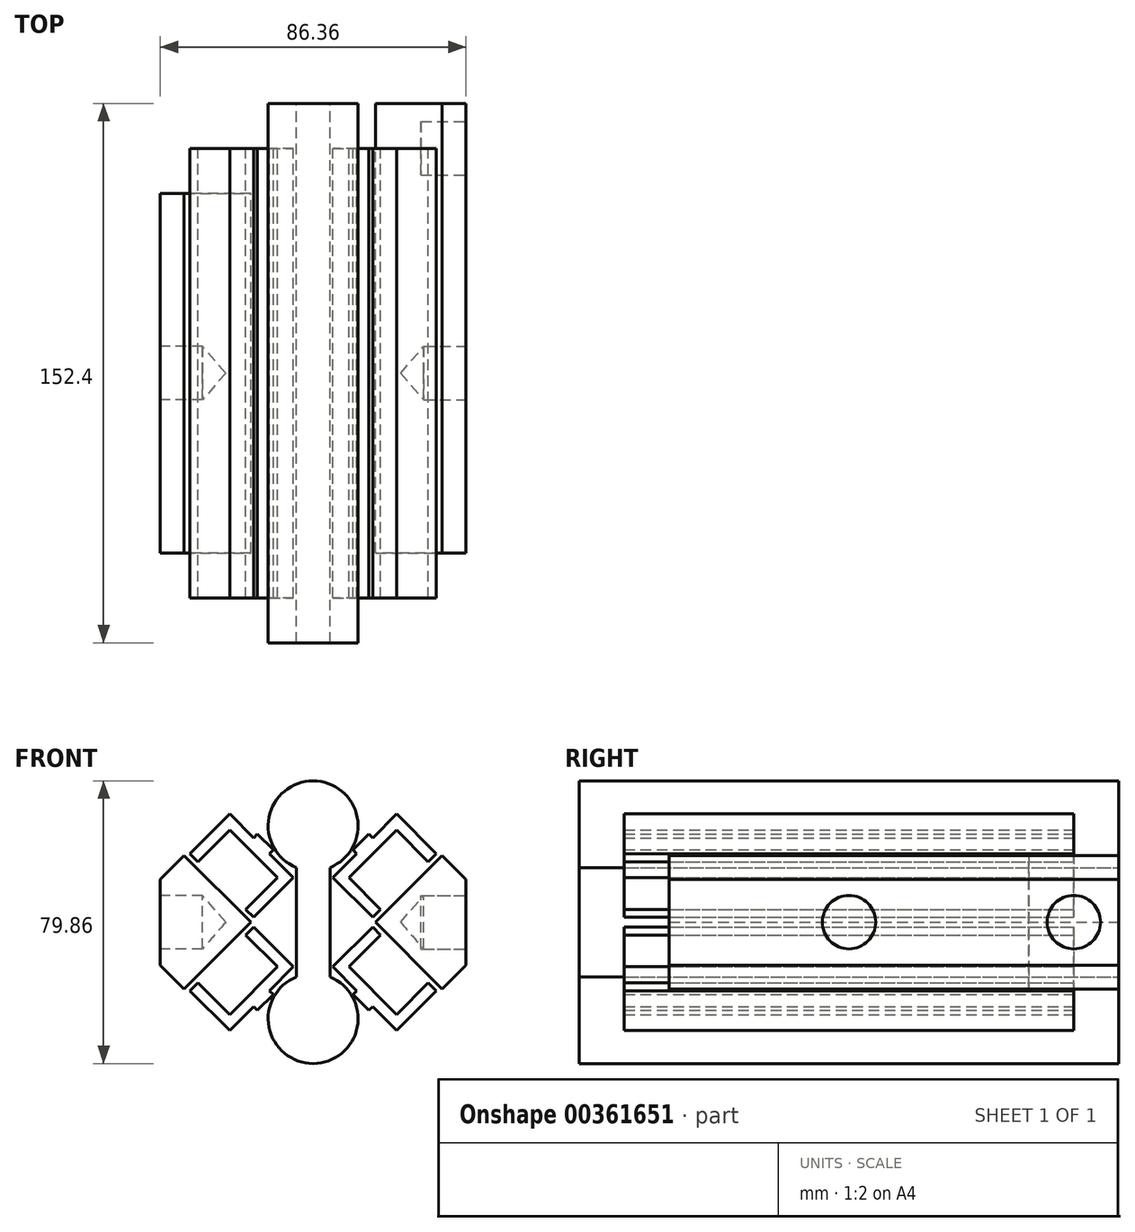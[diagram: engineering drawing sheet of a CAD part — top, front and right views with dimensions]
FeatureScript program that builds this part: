
annotation { "Feature Type Name" : "Feature", "Feature Type Description" : "" }
export const myFeature = defineFeature(function(context is Context, id is Id, definition is map)
    precondition{}
    {
        {
            var Q0;
            Q0=qCreatedBy(makeId("Front.planeOp"),FACE);
            var sketch = newSketch(context, id + "F0", { "sketchPlane" : qUnion([Q0])});
            skLineSegment(sketch, "E0", {"start": v(32.53, 17.1) * mm, "end": v(34.77, 19.34) * mm});
            skLineSegment(sketch, "E1", {"start": v(34.77, 19.34) * mm, "end": v(23.55, 30.57) * mm});
            skLineSegment(sketch, "E2", {"start": v(23.55, 30.57) * mm, "end": v(16.81, 23.84) * mm});
            skLineSegment(sketch, "E3", {"start": v(5.59, 12.6) * mm, "end": v(16.81, 1.38) * mm});
            skLineSegment(sketch, "E4", {"start": v(16.81, 1.38) * mm, "end": v(19.06, 3.63) * mm});
            skLineSegment(sketch, "E5", {"start": v(19.06, 3.63) * mm, "end": v(10.08, 12.6) * mm});
            skLineSegment(sketch, "E6", {"start": v(10.08, 12.6) * mm, "end": v(23.55, 26.08) * mm});
            skLineSegment(sketch, "E7", {"start": v(23.55, 26.08) * mm, "end": v(32.53, 17.1) * mm});
            skLineSegment(sketch, "E8", {"start": v(10.08, 12.6) * mm, "end": v(7.83, 10.36) * mm, "construction": true});
            skLineSegment(sketch, "E9", {"start": v(23.55, 26.08) * mm, "end": v(25.8, 28.33) * mm, "construction": true});
            skLineSegment(sketch, "E10", {"start": v(23.55, 26.08) * mm, "end": v(21.3, 28.33) * mm, "construction": true});
            skPoint(sketch, "E11", {"position": v(14.57, 21.6) * mm});
            skLineSegment(sketch, "E12", {"start": v(16.81, 23.84) * mm, "end": v(15.74, 24.91) * mm});
            skLineSegment(sketch, "E13", {"start": v(15.74, 24.91) * mm, "end": v(11.25, 20.42) * mm});
            skLineSegment(sketch, "E14", {"start": v(11.25, 20.42) * mm, "end": v(12.32, 19.34) * mm});
            skPoint(sketch, "E15", {"position": v(16.81, 19.34) * mm});
            skLineSegment(sketch, "E16.trimOffspring", {"start": v(12.32, 19.34) * mm, "end": v(5.59, 12.6) * mm});
            skLineSegment(sketch, "E17", {"start": v(16.81, 19.34) * mm, "end": v(-8.5, 44.65) * mm, "construction": true});
            skSolve(sketch);
        }
        {
            var Q0;
            Q0 = qSketchRegion(id + "F0", true);
            extrude(context, id + "F1", {"entities" : qUnion([Q0]), "endBound" : BoundingType.SYMMETRIC, "depth" : 127 * mm});
        }
        {
            var Q0;
            Q0=makeQuery(id+"F1.opExtrude","SWEPT_BODY",BODY,{"disambiguationData":[OSD([sQuery(id+"F0.wireOp",EDGE,"E0"),sQuery(id+"F0.wireOp",EDGE,"E1"),sQuery(id+"F0.wireOp",EDGE,"E2"),sQuery(id+"F0.wireOp",EDGE,"E3"),sQuery(id+"F0.wireOp",EDGE,"E4"),sQuery(id+"F0.wireOp",EDGE,"E5"),sQuery(id+"F0.wireOp",EDGE,"E6"),sQuery(id+"F0.wireOp",EDGE,"E7")])]});
            var Q1;
            Q1=qCreatedBy(makeId("Right.planeOp"),FACE);
            mirror(context, id + "F2", {"entities" : qUnion([Q0]), "mirrorPlane" : qUnion([Q1])});
        }
        {
            var Q0;
            Q0=makeQuery(id+"F1.opExtrude","SWEPT_BODY",BODY,{"disambiguationData":[OSD([sQuery(id+"F0.wireOp",EDGE,"E0"),sQuery(id+"F0.wireOp",EDGE,"E1"),sQuery(id+"F0.wireOp",EDGE,"E2"),sQuery(id+"F0.wireOp",EDGE,"E3"),sQuery(id+"F0.wireOp",EDGE,"E4"),sQuery(id+"F0.wireOp",EDGE,"E5"),sQuery(id+"F0.wireOp",EDGE,"E6"),sQuery(id+"F0.wireOp",EDGE,"E7")])]});
            var Q1;
            Q1=makeQuery(id+"F2.opPattern","COPY",BODY,{"derivedFrom":makeQuery(id+"F1.opExtrude","SWEPT_BODY",BODY,{"disambiguationData":[OSD([sQuery(id+"F0.wireOp",EDGE,"E0"),sQuery(id+"F0.wireOp",EDGE,"E1"),sQuery(id+"F0.wireOp",EDGE,"E2"),sQuery(id+"F0.wireOp",EDGE,"E3"),sQuery(id+"F0.wireOp",EDGE,"E4"),sQuery(id+"F0.wireOp",EDGE,"E5"),sQuery(id+"F0.wireOp",EDGE,"E6"),sQuery(id+"F0.wireOp",EDGE,"E7")])]}),"instanceName":"1"});
            var Q2;
            Q2=qCreatedBy(makeId("Top.planeOp"),FACE);
            mirror(context, id + "F3", {"entities" : qUnion([Q0, Q1]), "mirrorPlane" : qUnion([Q2])});
        }
        {
            var Q0;
            Q0=qCreatedBy(makeId("Front.planeOp"),FACE);
            var sketch = newSketch(context, id + "F4", { "sketchPlane" : qUnion([Q0])});
            skArc(sketch, "E18", {"start": v(4.76, 15.45) * mm, "mid": v(0, 39.93) * mm, "end": v(-4.76, 15.45) * mm});
            skArc(sketch, "E19", {"start": v(-4.76, -15.45) * mm, "mid": v(0, -39.93) * mm, "end": v(4.76, -15.45) * mm});
            skLineSegment(sketch, "E20.0", {"start": v(-12.32, 19.34) * mm, "end": v(-5.59, 12.6) * mm, "construction": true});
            skLineSegment(sketch, "E21.0", {"start": v(12.32, 19.34) * mm, "end": v(5.59, 12.6) * mm, "construction": true});
            skLineSegment(sketch, "E22.0", {"start": v(-12.32, -19.34) * mm, "end": v(-5.59, -12.6) * mm, "construction": true});
            skLineSegment(sketch, "E23.0", {"start": v(12.32, -19.34) * mm, "end": v(5.59, -12.6) * mm, "construction": true});
            skCircle(sketch, "E24", {"center": v(0, 0) * mm, "radius": 12.87 * mm, "construction": true});
            skLineSegment(sketch, "E25.0", {"start": v(-5.59, 12.6) * mm, "end": v(-16.81, 1.38) * mm, "construction": true});
            skLineSegment(sketch, "E26.0", {"start": v(5.59, 12.6) * mm, "end": v(16.81, 1.38) * mm, "construction": true});
            skLineSegment(sketch, "E27.0", {"start": v(5.59, -12.6) * mm, "end": v(16.81, -1.38) * mm, "construction": true});
            skLineSegment(sketch, "E28.0", {"start": v(-5.59, -12.6) * mm, "end": v(-16.81, -1.38) * mm, "construction": true});
            skLineSegment(sketch, "E29", {"start": v(0, 0) * mm, "end": v(58.9, 0) * mm, "construction": true});
            skLineSegment(sketch, "E30", {"start": v(5.59, 12.6) * mm, "end": v(-5.59, 12.6) * mm, "construction": true});
            skLineSegment(sketch, "E31", {"start": v(0, -27.23) * mm, "end": v(1.05, -31.6) * mm, "construction": true});
            skLineSegment(sketch, "E32", {"start": v(0, 12.6) * mm, "end": v(0, 2.94) * mm, "construction": true});
            skCircle(sketch, "E33", {"center": v(0, -27.23) * mm, "radius": 14.29 * mm, "construction": true});
            skLineSegment(sketch, "E34", {"start": v(-4.76, 15.45) * mm, "end": v(-4.76, -15.45) * mm});
            skLineSegment(sketch, "E35", {"start": v(4.76, 15.45) * mm, "end": v(4.76, -15.45) * mm});
            skSolve(sketch);
        }
        {
            var Q0;
            Q0 = qSketchRegion(id + "F4", true);
            extrude(context, id + "F5", {"entities" : qUnion([Q0]), "endBound" : BoundingType.SYMMETRIC, "depth" : 152.4 * mm, "offsetDistance" : 25.4 * mm});
        }
        {
            var Q0;
            Q0=qCreatedBy(makeId("Front.planeOp"),FACE);
            var sketch = newSketch(context, id + "F6", { "sketchPlane" : qUnion([Q0])});
            skArc(sketch, "E36", {"start": v(4.76, 17.75) * mm, "mid": v(0, 55.25) * mm, "end": v(-4.76, 17.75) * mm});
            skArc(sketch, "E37", {"start": v(-4.76, -17.75) * mm, "mid": v(0, -55.25) * mm, "end": v(4.76, -17.75) * mm});
            skLineSegment(sketch, "E38", {"start": v(4.76, 17.75) * mm, "end": v(4.76, -17.75) * mm});
            skLineSegment(sketch, "E39", {"start": v(-4.76, 17.75) * mm, "end": v(-4.76, -17.75) * mm});
            skLineSegment(sketch, "E40", {"start": v(0, 36.2) * mm, "end": v(0, -36.2) * mm, "construction": true});
            skLineSegment(sketch, "E41", {"start": v(41.06, 0) * mm, "end": v(-54.62, 0) * mm, "construction": true});
            skLineSegment(sketch, "E42.0", {"start": v(23.55, 30.57) * mm, "end": v(23.55, 30.57) * mm});
            skSolve(sketch);
        }
        {
            var Q0;
            Q0=qCreatedBy(makeId("Front.planeOp"),FACE);
            var sketch = newSketch(context, id + "F7", { "sketchPlane" : qUnion([Q0])});
            skPoint(sketch, "E43.0", {"position": v(16.81, 19.34) * mm});
            skPoint(sketch, "E44.0", {"position": v(16.81, -19.34) * mm});
            skLineSegment(sketch, "E45", {"start": v(16.81, 19.34) * mm, "end": v(36.16, 0) * mm, "construction": true});
            skLineSegment(sketch, "E46", {"start": v(36.16, 0) * mm, "end": v(16.81, -19.34) * mm, "construction": true});
            skLineSegment(sketch, "E47", {"start": v(36.16, 0) * mm, "end": v(65.23, 0) * mm, "construction": true});
            skLineSegment(sketch, "E48", {"start": v(43.18, 12.12) * mm, "end": v(43.18, -12.12) * mm});
            skLineSegment(sketch, "E49", {"start": v(43.18, -12.12) * mm, "end": v(36.44, -18.86) * mm});
            skLineSegment(sketch, "E50", {"start": v(36.44, -18.86) * mm, "end": v(17.58, 0) * mm});
            skLineSegment(sketch, "E51", {"start": v(17.58, 0) * mm, "end": v(36.44, 18.86) * mm});
            skLineSegment(sketch, "E52", {"start": v(36.44, 18.86) * mm, "end": v(43.18, 12.12) * mm});
            skPoint(sketch, "E53.0", {"position": v(33.65, 18.22) * mm});
            skPoint(sketch, "E54.0", {"position": v(29.16, 24.96) * mm});
            skSolve(sketch);
        }
        {
            var Q0;
            Q0 = qSketchRegion(id + "F7", true);
            extrude(context, id + "F8", {"entities" : qUnion([Q0]), "endBound" : BoundingType.SYMMETRIC, "depth" : 101.6 * mm});
        }
        {
            var Q0;
            Q0=qCreatedBy(makeId("Front.planeOp"),FACE);
            var sketch = newSketch(context, id + "F9", { "sketchPlane" : qUnion([Q0])});
            skLineSegment(sketch, "E55", {"start": v(43.18, 0) * mm, "end": v(43.18, 7.54) * mm});
            skLineSegment(sketch, "E56", {"start": v(43.18, 7.54) * mm, "end": v(31.24, 7.54) * mm});
            skLineSegment(sketch, "E57", {"start": v(31.24, 7.54) * mm, "end": v(24.68, 0) * mm});
            skLineSegment(sketch, "E58", {"start": v(24.68, 0) * mm, "end": v(43.18, 0) * mm});
            skSolve(sketch);
        }
        {
            var Q0;
            Q0 = qSketchRegion(id + "F9", true);
            var Q1;
            Q1=sQuery(id+"F9.wireOp",EDGE,"E58");
            revolve(context, id + "F10", {"operationType" : NewBodyOperationType.REMOVE, "entities" : qUnion([Q0]), "axis" : qUnion([Q1]), "revolveType" : RevolveType.FULL, "oppositeDirection" : true});
        }
        {
            var Q0;
            Q0=makeQuery(id+"F8.opExtrude","SWEPT_BODY",BODY,{"disambiguationData":[OSD([sQuery(id+"F7.wireOp",EDGE,"E48"),sQuery(id+"F7.wireOp",EDGE,"E49"),sQuery(id+"F7.wireOp",EDGE,"E50"),sQuery(id+"F7.wireOp",EDGE,"E51"),sQuery(id+"F7.wireOp",EDGE,"E52")])]});
            var Q1;
            Q1=qCreatedBy(makeId("Right.planeOp"),FACE);
            mirror(context, id + "F11", {"entities" : qUnion([Q0]), "mirrorPlane" : qUnion([Q1])});
        }
        {
            var Q0;
            Q0=makeQuery(id+"F8.opExtrude","CAP_FACE",FACE,{"disambiguationData":[OSD([sQuery(id+"F7.wireOp",EDGE,"E48"),sQuery(id+"F7.wireOp",EDGE,"E49"),sQuery(id+"F7.wireOp",EDGE,"E50"),sQuery(id+"F7.wireOp",EDGE,"E51"),sQuery(id+"F7.wireOp",EDGE,"E52")])],"isStart":true});
            var sketch = newSketch(context, id + "F12", { "sketchPlane" : qUnion([Q0])});
            skLineSegment(sketch, "E59.0", {"start": v(-43.18, 12.12) * mm, "end": v(-43.18, -12.12) * mm});
            skLineSegment(sketch, "E60.0", {"start": v(-17.58, 0) * mm, "end": v(-36.44, 18.86) * mm});
            skLineSegment(sketch, "E61.0", {"start": v(-36.44, -18.86) * mm, "end": v(-17.58, 0) * mm});
            skLineSegment(sketch, "E62.0", {"start": v(-43.18, -12.12) * mm, "end": v(-36.44, -18.86) * mm});
            skLineSegment(sketch, "E63.0", {"start": v(-36.44, 18.86) * mm, "end": v(-43.18, 12.12) * mm});
            skSolve(sketch);
        }
        {
            var Q0;
            Q0 = qSketchRegion(id + "F12", true);
            extrude(context, id + "F13", {"entities" : qUnion([Q0]), "operationType" : NewBodyOperationType.ADD, "depth" : 25.4 * mm, "offsetDistance" : 25.4 * mm});
        }
        {
            var Q0;
            Q0=makeQuery(id+"F8.opExtrude","SWEPT_FACE",FACE,{"disambiguationData":[OSD([sQuery(id+"F7.wireOp",EDGE,"E48")])]});
            var sketch = newSketch(context, id + "F14", { "sketchPlane" : qUnion([Q0])});
            skCircle(sketch, "E64.0", {"center": v(0, 0) * mm, "radius": 7.54 * mm, "construction": true});
            skLineSegment(sketch, "E65", {"start": v(0, 0) * mm, "end": v(63.5, 0) * mm, "construction": true});
            skPoint(sketch, "E65.endSnap0", {"position": v(50.8, 0) * mm});
            skCircle(sketch, "E66", {"center": v(63.5, 0) * mm, "radius": 7.54 * mm});
            skLineSegment(sketch, "E67.0", {"start": v(-50.8, 12.12) * mm, "end": v(76.2, 12.12) * mm, "construction": true});
            skSolve(sketch);
        }
        {
            var Q0;
            Q0 = qSketchRegion(id + "F14", true);
            extrude(context, id + "F15", {"entities" : qUnion([Q0]), "operationType" : NewBodyOperationType.REMOVE, "oppositeDirection" : true, "depth" : 12.7 * mm, "offsetDistance" : 25.4 * mm});
        }
    });
